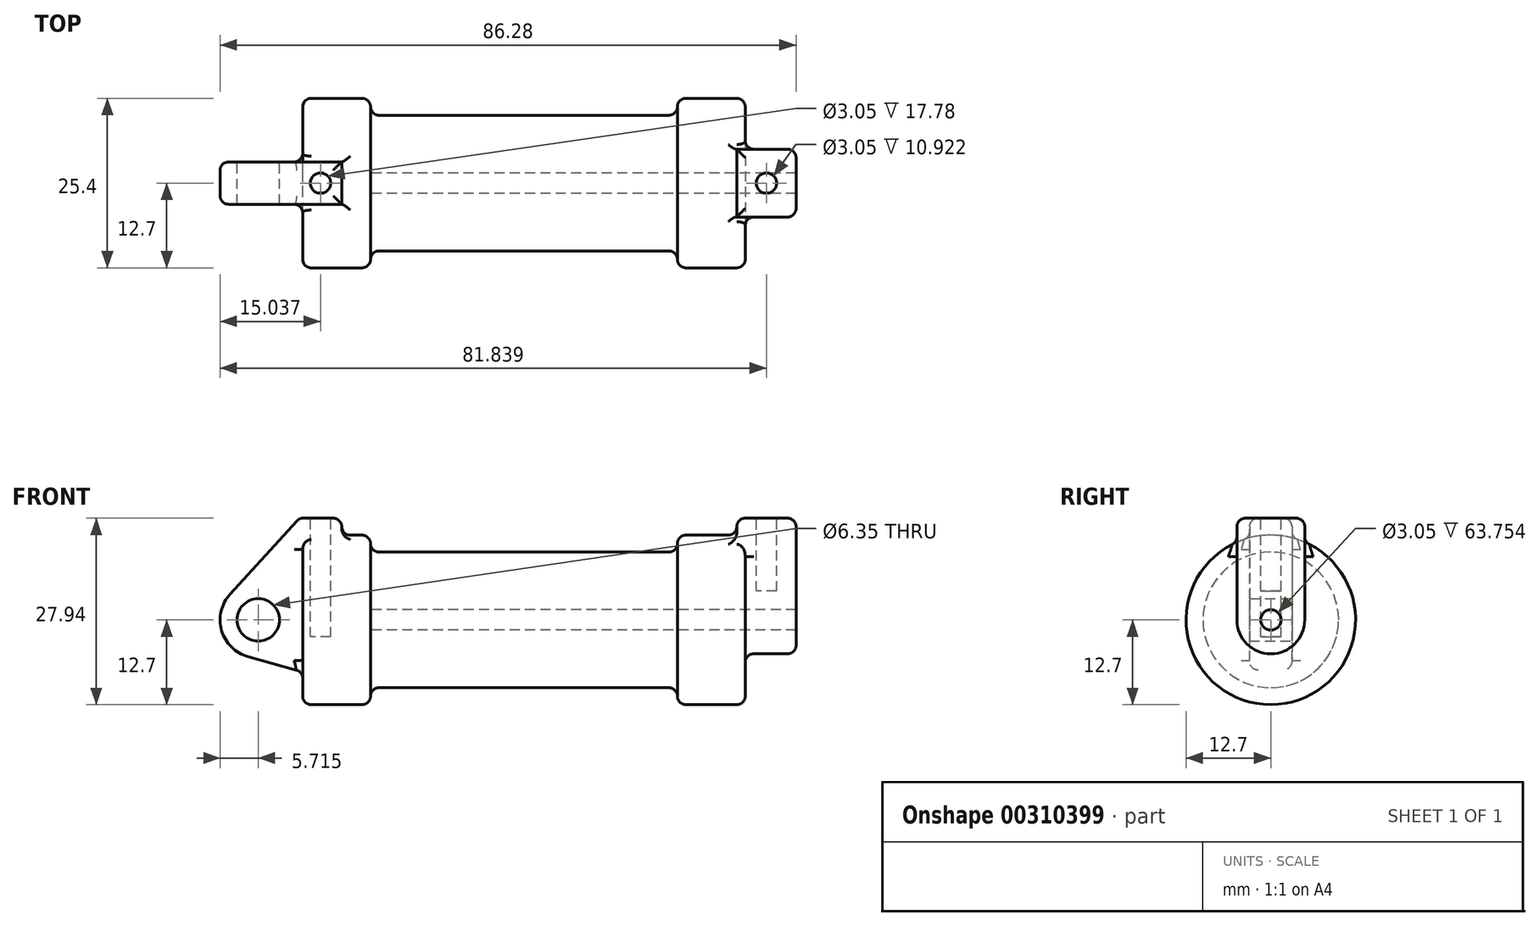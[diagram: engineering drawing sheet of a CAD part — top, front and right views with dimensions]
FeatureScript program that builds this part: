
annotation { "Feature Type Name" : "Feature", "Feature Type Description" : "" }
export const myFeature = defineFeature(function(context is Context, id is Id, definition is map)
    precondition{}
    {
        {
            var Q0;
            Q0=qCreatedBy(makeId("Front.planeOp"),FACE);
            var sketch = newSketch(context, id + "F0", { "sketchPlane" : qUnion([Q0])});
            skLineSegment(sketch, "E0", {"start": v(0, 0) * mm, "end": v(0, 12.7) * mm});
            skLineSegment(sketch, "E1", {"start": v(0, 12.7) * mm, "end": v(10.16, 12.7) * mm});
            skLineSegment(sketch, "E2", {"start": v(10.16, 12.7) * mm, "end": v(10.16, 10.16) * mm});
            skLineSegment(sketch, "E3", {"start": v(10.16, 10.16) * mm, "end": v(56.13, 10.16) * mm});
            skLineSegment(sketch, "E4", {"start": v(56.13, 10.16) * mm, "end": v(56.13, 12.7) * mm});
            skLineSegment(sketch, "E5", {"start": v(56.13, 12.7) * mm, "end": v(66.3, 12.7) * mm});
            skLineSegment(sketch, "E6", {"start": v(66.3, 12.7) * mm, "end": v(66.3, 0) * mm});
            skLineSegment(sketch, "E7", {"start": v(66.3, 0) * mm, "end": v(0, 0) * mm});
            skLineSegment(sketch, "E8", {"start": v(5.84, 15.24) * mm, "end": v(-0.5, 15.24) * mm});
            skLineSegment(sketch, "E9", {"start": v(-0.5, 15.24) * mm, "end": v(-10.88, 3.85) * mm});
            skLineSegment(sketch, "E10", {"start": v(0, 0) * mm, "end": v(-6.65, 0) * mm});
            skCircle(sketch, "E11", {"center": v(-6.65, 0) * mm, "radius": 5.72 * mm});
            skCircle(sketch, "E12", {"center": v(-6.65, 0) * mm, "radius": 3.18 * mm});
            skLineSegment(sketch, "E13", {"start": v(5.84, 15.24) * mm, "end": v(5.84, -9.4) * mm});
            skLineSegment(sketch, "E14", {"start": v(5.84, -9.4) * mm, "end": v(-8.18, -5.5) * mm});
            skLineSegment(sketch, "E15", {"start": v(0, 9.37) * mm, "end": v(5.84, 9.37) * mm});
            skSolve(sketch);
        }
        {
            var Q0;
            {var subQ0=sQuery(id+"F0.wireOp",EDGE,"E0");Q0=makeQuery(id+"F0.imprint","IMPRINT",FACE,{"disambiguationData":[TD([[makeQuery(id+"F0.imprint","IMPRINT",EDGE,{"derivedFrom":subQ0}),-1.0]])]});}
            var Q1;
            {var subQ0=sQuery(id+"F0.wireOp",EDGE,"E2");Q1=makeQuery(id+"F0.imprint","IMPRINT",FACE,{"disambiguationData":[TD([[makeQuery(id+"F0.imprint","IMPRINT",EDGE,{"derivedFrom":subQ0}),-1.0]])]});}
            var Q2;
            Q2=sQuery(id+"F0.wireOp",EDGE,"E7");
            revolve(context, id + "F1", {"entities" : qUnion([Q0, Q1]), "axis" : qUnion([Q2]), "revolveType" : RevolveType.FULL});
        }
        {
            var Q0;
            {var subQ3=sQuery(id+"F0.wireOp",EDGE,"E15");Q0=makeQuery(id+"F0.imprint","IMPRINT",FACE,{"disambiguationData":[TD([[makeQuery(id+"F0.imprint","IMPRINT",EDGE,{"derivedFrom":subQ3}),1.0]])]});}
            var Q1;
            {var subQ9=sQuery(id+"F0.wireOp",EDGE,"E8");Q1=makeQuery(id+"F0.imprint","IMPRINT",FACE,{"disambiguationData":[TD([[makeQuery(id+"F0.imprint","IMPRINT",EDGE,{"derivedFrom":subQ9}),1.0]])]});}
            var Q2;
            {var subQ0=sQuery(id+"F0.wireOp",EDGE,"E14");Q2=makeQuery(id+"F0.imprint","IMPRINT",FACE,{"disambiguationData":[TD([[makeQuery(id+"F0.imprint","IMPRINT",EDGE,{"derivedFrom":subQ0}),-1.0]])]});}
            var Q3;
            Q3=makeQuery(id+"F0.imprint","IMPRINT",FACE,{"disambiguationData":[TD([[makeQuery(id+"F0.imprint","IMPRINT",EDGE,{"derivedFrom":sQuery(id+"F0.wireOp",EDGE,"E12")}),-1.0]])]});
            extrude(context, id + "F2", {"entities" : qUnion([Q0, Q1, Q2, Q3]), "operationType" : NewBodyOperationType.ADD, "endBound" : BoundingType.SYMMETRIC, "depth" : 6.35 * mm});
        }
        {
            var Q0;
            Q0=makeQuery(id+"F1.opRevolve","SWEPT_FACE",FACE,{"disambiguationData":[OSD([sQuery(id+"F0.wireOp",EDGE,"E6")])]});
            var sketch = newSketch(context, id + "F3", { "sketchPlane" : qUnion([Q0])});
            skCircle(sketch, "E16", {"center": v(0, 0) * mm, "radius": 5.08 * mm});
            skCircle(sketch, "E17", {"center": v(0, 0) * mm, "radius": 1.52 * mm});
            skLineSegment(sketch, "E18", {"start": v(5.08, 0) * mm, "end": v(5.08, 15.24) * mm});
            skLineSegment(sketch, "E19", {"start": v(-5.08, 0) * mm, "end": v(-5.08, 15.24) * mm});
            skLineSegment(sketch, "E20", {"start": v(-5.08, 15.24) * mm, "end": v(5.08, 15.24) * mm});
            skSolve(sketch);
        }
        {
            var Q0;
            {var subQ0=sQuery(id+"F3.wireOp",EDGE,"E20");Q0=makeQuery(id+"F3.imprint","IMPRINT",FACE,{"disambiguationData":[TD([[makeQuery(id+"F3.imprint","IMPRINT",EDGE,{"derivedFrom":subQ0}),-1.0]])]});}
            var Q1;
            {var subQ0=sQuery(id+"F3.wireOp",EDGE,"E18");var subQ1=sQuery(id+"F3.wireOp",EDGE,"E16");var subQ2=makeQuery(id+"F3.imprint","INTERSECT",VERTEX,{"derivedFrom":[subQ1,subQ0]});Q1=makeQuery(id+"F3.imprint","IMPRINT",FACE,{"disambiguationData":[TD([[makeQuery(id+"F3.imprint","IMPRINT",EDGE,{"disambiguationData":[TD([[subQ2,-1.0]])],"derivedFrom":subQ1}),-1.0]])]});}
            var Q2;
            Q2=makeQuery(id+"F3.imprint","IMPRINT",FACE,{"disambiguationData":[TD([[makeQuery(id+"F3.imprint","IMPRINT",EDGE,{"derivedFrom":sQuery(id+"F3.wireOp",EDGE,"E17")}),-1.0]])]});
            extrude(context, id + "F4", {"entities" : qUnion([Q0, Q1, Q2]), "operationType" : NewBodyOperationType.ADD, "depth" : 7.62 * mm, "hasSecondDirection" : true, "secondDirectionOppositeDirection" : true, "secondDirectionDepth" : 1.27 * mm});
        }
        {
            var Q0;
            Q0=makeQuery(id+"F4.boolean.opBoolean","SPLIT",FACE,{"disambiguationData":[TD([makeQuery(id+"F4.opExtrude","SWEPT_FACE",FACE,{"disambiguationData":[OSD([sQuery(id+"F3.wireOp",EDGE,"E17")])]})])],"derivedFrom":makeQuery(id+"F1.opRevolve","SWEPT_FACE",FACE,{"disambiguationData":[OSD([sQuery(id+"F0.wireOp",EDGE,"E6")])]})});
            var Q1;
            Q1=makeQuery(id+"F1.opRevolve","SWEPT_FACE",FACE,{"disambiguationData":[OSD([sQuery(id+"F0.wireOp",EDGE,"E2")])]});
            extrude(context, id + "F5", {"entities" : qUnion([Q0]), "operationType" : NewBodyOperationType.REMOVE, "endBound" : BoundingType.UP_TO_SURFACE, "oppositeDirection" : true, "endBoundEntityFace" : qUnion([Q1]), "depth" : 25.4 * mm});
        }
        {
            var Q0;
            Q0=makeQuery(id+"F4.opExtrude","SWEPT_FACE",FACE,{"disambiguationData":[OSD([sQuery(id+"F3.wireOp",EDGE,"E20")])]});
            var sketch = newSketch(context, id + "F6", { "sketchPlane" : qUnion([Q0])});
            skLineSegment(sketch, "E21", {"start": v(69.47, 5.08) * mm, "end": v(69.47, -5.08) * mm, "construction": true});
            skLineSegment(sketch, "E22", {"start": v(65.02, 0) * mm, "end": v(69.47, 0) * mm, "construction": true});
            skCircle(sketch, "E23", {"center": v(69.47, 0) * mm, "radius": 1.52 * mm});
            skSolve(sketch);
        }
        {
            var Q0;
            Q0=makeQuery(id+"F2.opExtrude","SWEPT_FACE",FACE,{"disambiguationData":[OSD([sQuery(id+"F0.wireOp",EDGE,"E8")])]});
            var sketch = newSketch(context, id + "F7", { "sketchPlane" : qUnion([Q0])});
            skLineSegment(sketch, "E24", {"start": v(2.67, 3.18) * mm, "end": v(2.67, -3.18) * mm, "construction": true});
            skLineSegment(sketch, "E25", {"start": v(2.67, 0) * mm, "end": v(5.84, 0) * mm, "construction": true});
            skCircle(sketch, "E26", {"center": v(2.67, 0) * mm, "radius": 1.52 * mm});
            skSolve(sketch);
        }
        {
            var Q0;
            Q0=makeQuery(id+"F7.imprint","IMPRINT",FACE,{"disambiguationData":[TD([[makeQuery(id+"F7.imprint","IMPRINT",EDGE,{"derivedFrom":sQuery(id+"F7.wireOp",EDGE,"E26")}),1.0]])]});
            extrude(context, id + "F8", {"entities" : qUnion([Q0]), "operationType" : NewBodyOperationType.REMOVE, "oppositeDirection" : true, "depth" : 17.78 * mm});
        }
        {
            var Q0;
            Q0=makeQuery(id+"F6.imprint","IMPRINT",FACE,{"disambiguationData":[TD([[makeQuery(id+"F6.imprint","IMPRINT",EDGE,{"derivedFrom":sQuery(id+"F6.wireOp",EDGE,"E23")}),1.0]])]});
            extrude(context, id + "F9", {"entities" : qUnion([Q0]), "operationType" : NewBodyOperationType.REMOVE, "oppositeDirection" : true, "depth" : 10.92 * mm});
        }
        {
            var Q0;
            Q0=makeQuery(id+"F1.opRevolve","SWEPT_EDGE",EDGE,{"disambiguationData":[OSD([sQuery(id+"F0.wireOp",EDGE,"E3"),sQuery(id+"F0.wireOp",EDGE,"E4")])]});
            var Q1;
            Q1=makeQuery(id+"F1.opRevolve","SWEPT_EDGE",EDGE,{"disambiguationData":[OSD([sQuery(id+"F0.wireOp",EDGE,"E4"),sQuery(id+"F0.wireOp",EDGE,"E5")])]});
            var Q2;
            Q2=makeQuery(id+"F1.opRevolve","SWEPT_EDGE",EDGE,{"disambiguationData":[OSD([sQuery(id+"F0.wireOp",EDGE,"E2"),sQuery(id+"F0.wireOp",EDGE,"E3")])]});
            var Q3;
            Q3=makeQuery(id+"F1.opRevolve","SWEPT_EDGE",EDGE,{"disambiguationData":[OSD([sQuery(id+"F0.wireOp",EDGE,"E1"),sQuery(id+"F0.wireOp",EDGE,"E2")])]});
            var Q4;
            Q4=makeQuery(id+"F1.opRevolve","SWEPT_EDGE",EDGE,{"disambiguationData":[OSD([sQuery(id+"F0.wireOp",EDGE,"E5"),sQuery(id+"F0.wireOp",EDGE,"E6")])]});
            var Q5;
            Q5=makeQuery(id+"F1.opRevolve","SWEPT_EDGE",EDGE,{"disambiguationData":[OSD([sQuery(id+"F0.wireOp",EDGE,"E0"),sQuery(id+"F0.wireOp",EDGE,"E1")])]});
            fillet(context, id + "F10", {"entities" : qUnion([Q0, Q1, Q2, Q3, Q4, Q5]), "radius" : 1.27 * mm, "tangentPropagation" : true, "allowEdgeOverflow" : false});
        }
        {
            var Q0;
            {var subQ0=sQuery(id+"F0.wireOp",EDGE,"E0");Q0=makeQuery(id+"F2.boolean.opBoolean","INTERSECT",EDGE,{"derivedFrom":[makeQuery(id+"F1.opRevolve","SWEPT_FACE",FACE,{"disambiguationData":[OSD([subQ0])]}),makeQuery(id+"F2.opExtrude","CAP_FACE",FACE,{"disambiguationData":[OSD([subQ0,sQuery(id+"F0.wireOp",EDGE,"E7"),sQuery(id+"F0.wireOp",EDGE,"E8"),sQuery(id+"F0.wireOp",EDGE,"E9"),sQuery(id+"F0.wireOp",EDGE,"E11"),sQuery(id+"F0.wireOp",EDGE,"E12"),sQuery(id+"F0.wireOp",EDGE,"E13"),sQuery(id+"F0.wireOp",EDGE,"E14"),sQuery(id+"F0.wireOp",EDGE,"E15")])],"isStart":false})]});}
            var Q1;
            {var subQ0=sQuery(id+"F0.wireOp",EDGE,"E0");Q1=makeQuery(id+"F2.boolean.opBoolean","INTERSECT",EDGE,{"derivedFrom":[makeQuery(id+"F1.opRevolve","SWEPT_FACE",FACE,{"disambiguationData":[OSD([subQ0])]}),makeQuery(id+"F2.opExtrude","CAP_FACE",FACE,{"disambiguationData":[OSD([subQ0,sQuery(id+"F0.wireOp",EDGE,"E7"),sQuery(id+"F0.wireOp",EDGE,"E8"),sQuery(id+"F0.wireOp",EDGE,"E9"),sQuery(id+"F0.wireOp",EDGE,"E11"),sQuery(id+"F0.wireOp",EDGE,"E12"),sQuery(id+"F0.wireOp",EDGE,"E13"),sQuery(id+"F0.wireOp",EDGE,"E14"),sQuery(id+"F0.wireOp",EDGE,"E15")])],"isStart":true})]});}
            var Q2;
            Q2=makeQuery(id+"F2.boolean.opBoolean","INTERSECT",EDGE,{"derivedFrom":[makeQuery(id+"F1.opRevolve","SWEPT_FACE",FACE,{"disambiguationData":[OSD([sQuery(id+"F0.wireOp",EDGE,"E0")])]}),makeQuery(id+"F2.opExtrude","SWEPT_FACE",FACE,{"disambiguationData":[OSD([sQuery(id+"F0.wireOp",EDGE,"E14")])]})]});
            var Q3;
            {var subQ0=sQuery(id+"F0.wireOp",EDGE,"E13");var subQ1=sQuery(id+"F0.wireOp",EDGE,"E1");Q3=makeQuery(id+"F2.boolean.opBoolean","INTERSECT",EDGE,{"derivedFrom":[makeQuery(id+"F1.opRevolve","SWEPT_FACE",FACE,{"disambiguationData":[OSD([subQ1])]}),makeQuery(id+"F2.opExtrude","SWEPT_FACE",FACE,{"disambiguationData":[OSD([subQ0]),TDD([makeQuery(id+"F0.imprint","IMPRINT",EDGE,{"disambiguationData":[TD([[makeQuery(id+"F0.imprint","INTERSECT",VERTEX,{"derivedFrom":[sQuery(id+"F0.wireOp",EDGE,"E8"),subQ0]}),-1.0]])],"derivedFrom":subQ0}),makeQuery(id+"F0.imprint","IMPRINT",EDGE,{"disambiguationData":[TD([[makeQuery(id+"F0.imprint","INTERSECT",VERTEX,{"derivedFrom":[subQ0,sQuery(id+"F0.wireOp",EDGE,"E15")]}),1.0]])],"derivedFrom":subQ0})])]})]});}
            var Q4;
            Q4=makeQuery(id+"F2.opExtrude","CAP_EDGE",EDGE,{"disambiguationData":[OSD([sQuery(id+"F0.wireOp",EDGE,"E9")])],"isStart":false});
            var Q5;
            Q5=makeQuery(id+"F2.opExtrude","CAP_EDGE",EDGE,{"disambiguationData":[OSD([sQuery(id+"F0.wireOp",EDGE,"E9")])],"isStart":true});
            var Q6;
            Q6=makeQuery(id+"F2.opExtrude","SWEPT_EDGE",EDGE,{"disambiguationData":[OSD([sQuery(id+"F0.wireOp",EDGE,"E8"),sQuery(id+"F0.wireOp",EDGE,"E13")])]});
            var Q7;
            Q7=makeQuery(id+"F2.opExtrude","CAP_EDGE",EDGE,{"disambiguationData":[OSD([sQuery(id+"F0.wireOp",EDGE,"E8")])],"isStart":false});
            var Q8;
            Q8=makeQuery(id+"F2.opExtrude","CAP_EDGE",EDGE,{"disambiguationData":[OSD([sQuery(id+"F0.wireOp",EDGE,"E8")])],"isStart":true});
            var Q9;
            Q9=makeQuery(id+"F2.opExtrude","SWEPT_EDGE",EDGE,{"disambiguationData":[OSD([sQuery(id+"F0.wireOp",EDGE,"E8"),sQuery(id+"F0.wireOp",EDGE,"E9")])]});
            fillet(context, id + "F11", {"entities" : qUnion([Q0, Q1, Q2, Q3, Q4, Q5, Q6, Q7, Q8, Q9]), "radius" : 1.27 * mm, "tangentPropagation" : true, "allowEdgeOverflow" : false});
        }
        {
            var Q0;
            Q0=makeQuery(id+"F4.opExtrude","CAP_EDGE",EDGE,{"disambiguationData":[OSD([sQuery(id+"F3.wireOp",EDGE,"E18")])],"isStart":false});
            var Q1;
            Q1=makeQuery(id+"F4.opExtrude","CAP_EDGE",EDGE,{"disambiguationData":[OSD([sQuery(id+"F3.wireOp",EDGE,"E20")])],"isStart":false});
            var Q2;
            Q2=makeQuery(id+"F4.opExtrude","SWEPT_EDGE",EDGE,{"disambiguationData":[OSD([sQuery(id+"F3.wireOp",EDGE,"E18"),sQuery(id+"F3.wireOp",EDGE,"E20")])]});
            var Q3;
            Q3=makeQuery(id+"F4.opExtrude","CAP_EDGE",EDGE,{"disambiguationData":[OSD([sQuery(id+"F3.wireOp",EDGE,"E20")])],"isStart":true});
            var Q4;
            Q4=makeQuery(id+"F4.opExtrude","SWEPT_EDGE",EDGE,{"disambiguationData":[OSD([sQuery(id+"F3.wireOp",EDGE,"E19"),sQuery(id+"F3.wireOp",EDGE,"E20")])]});
            var Q5;
            Q5=makeQuery(id+"F4.boolean.opBoolean","INTERSECT",EDGE,{"derivedFrom":[makeQuery(id+"F1.opRevolve","SWEPT_FACE",FACE,{"disambiguationData":[OSD([sQuery(id+"F0.wireOp",EDGE,"E6")])]}),makeQuery(id+"F4.opExtrude","SWEPT_FACE",FACE,{"disambiguationData":[OSD([sQuery(id+"F3.wireOp",EDGE,"E19")])]})]});
            var Q6;
            Q6=makeQuery(id+"F4.boolean.opBoolean","INTERSECT",EDGE,{"derivedFrom":[makeQuery(id+"F1.opRevolve","SWEPT_FACE",FACE,{"disambiguationData":[OSD([sQuery(id+"F0.wireOp",EDGE,"E5")])]}),makeQuery(id+"F4.opExtrude","CAP_FACE",FACE,{"disambiguationData":[OSD([sQuery(id+"F3.wireOp",EDGE,"E16"),sQuery(id+"F3.wireOp",EDGE,"E17"),sQuery(id+"F3.wireOp",EDGE,"E18"),sQuery(id+"F3.wireOp",EDGE,"E19"),sQuery(id+"F3.wireOp",EDGE,"E20")])],"isStart":true})]});
            fillet(context, id + "F12", {"entities" : qUnion([Q0, Q1, Q2, Q3, Q4, Q5, Q6]), "radius" : 1.27 * mm, "tangentPropagation" : true, "allowEdgeOverflow" : false});
        }
    });
